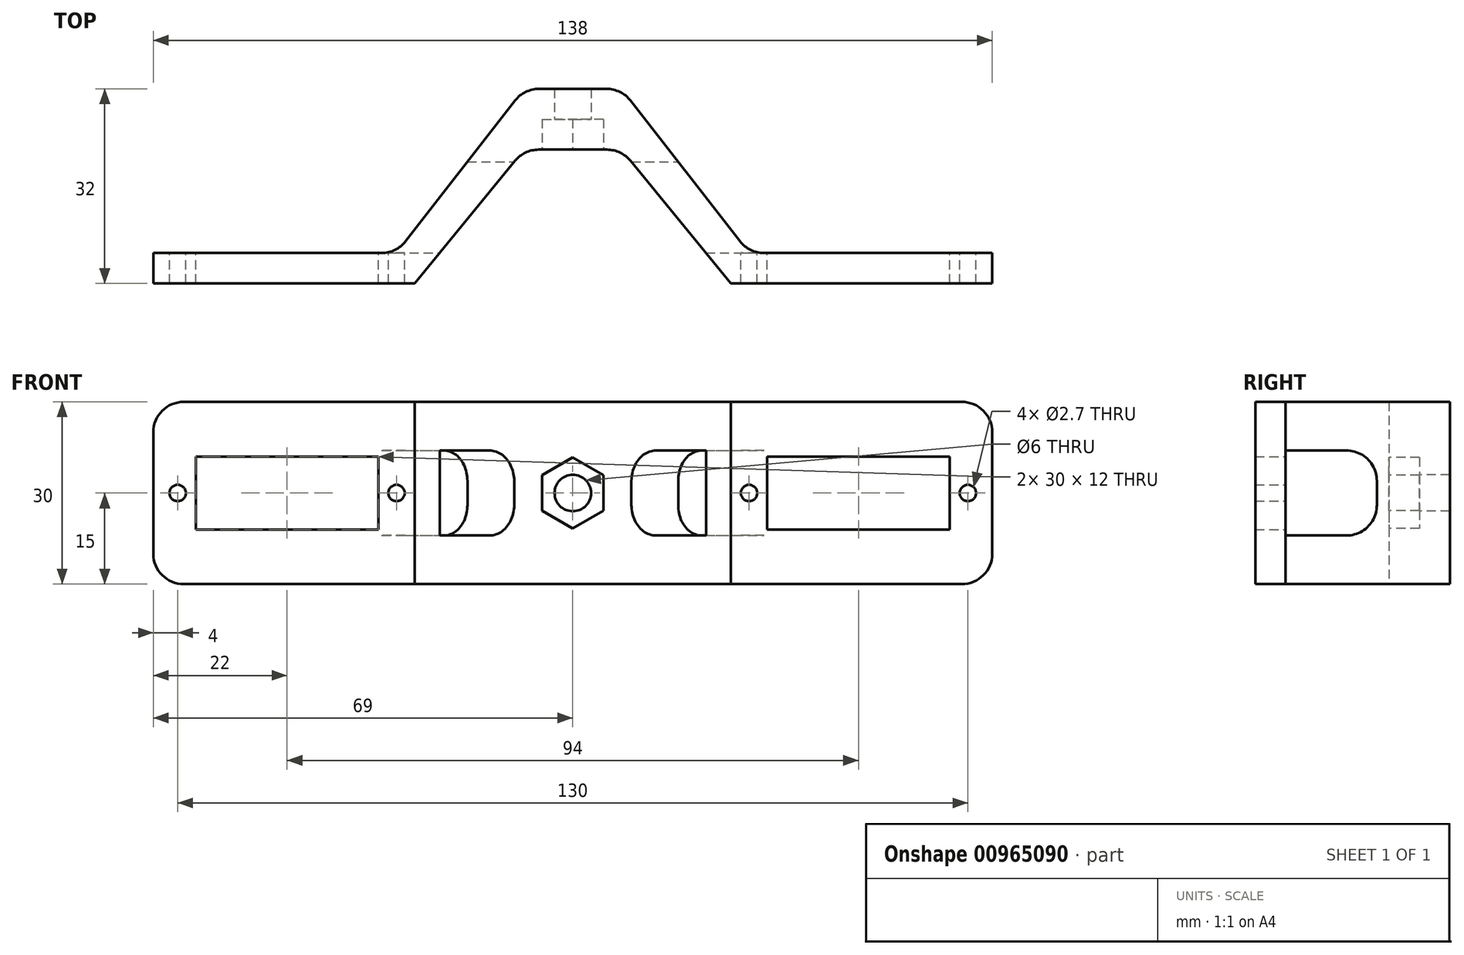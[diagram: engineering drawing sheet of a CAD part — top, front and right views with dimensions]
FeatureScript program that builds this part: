
annotation { "Feature Type Name" : "Feature", "Feature Type Description" : "" }
export const myFeature = defineFeature(function(context is Context, id is Id, definition is map)
    precondition{}
    {
        {
            var Q0;
            Q0=qCreatedBy(makeId("Top.planeOp"),FACE);
            var sketch = newSketch(context, id + "F0", { "sketchPlane" : qUnion([Q0])});
            skLineSegment(sketch, "E0", {"start": v(8, 32) * mm, "end": v(-8, 32) * mm});
            skLineSegment(sketch, "E1", {"start": v(-8, 32) * mm, "end": v(-29, 5) * mm});
            skLineSegment(sketch, "E2", {"start": v(-29, 5) * mm, "end": v(-69, 5) * mm});
            skLineSegment(sketch, "E3", {"start": v(-69, 5) * mm, "end": v(-69, 0) * mm});
            skLineSegment(sketch, "E4", {"start": v(69, 0) * mm, "end": v(69, 5) * mm});
            skLineSegment(sketch, "E5", {"start": v(69, 5) * mm, "end": v(29, 5) * mm});
            skLineSegment(sketch, "E6", {"start": v(29, 5) * mm, "end": v(8, 32) * mm});
            skLineSegment(sketch, "E7", {"start": v(-69, 0) * mm, "end": v(-26, 0) * mm});
            skLineSegment(sketch, "E8", {"start": v(-26, 0) * mm, "end": v(-8, 22) * mm});
            skLineSegment(sketch, "E9", {"start": v(-8, 22) * mm, "end": v(8, 22) * mm});
            skLineSegment(sketch, "E10", {"start": v(8, 22) * mm, "end": v(26, 0) * mm});
            skLineSegment(sketch, "E11", {"start": v(26, 0) * mm, "end": v(69, 0) * mm});
            skSolve(sketch);
        }
        {
            var Q0;
            Q0=makeQuery(id+"F0.imprint","IMPRINT",FACE,{"disambiguationData":[TD([[makeQuery(id+"F0.imprint","IMPRINT",EDGE,{"derivedFrom":sQuery(id+"F0.wireOp",EDGE,"E0")}),1.0]])]});
            extrude(context, id + "F1", {"entities" : qUnion([Q0]), "flatOperationType" : FlatOperationType.REMOVE, "depth" : 30 * mm, "offsetDistance" : 25 * mm, "domain" : OperationDomain.MODEL});
        }
        {
            var Q0;
            Q0=makeQuery(id+"F1.opExtrude","SWEPT_FACE",FACE,{"disambiguationData":[OSD([sQuery(id+"F0.wireOp",EDGE,"E5")])]});
            var sketch = newSketch(context, id + "F2", { "sketchPlane" : qUnion([Q0])});
            skLineSegment(sketch, "E12.bottom", {"start": v(62, 9) * mm, "end": v(32, 9) * mm});
            skLineSegment(sketch, "E12.top", {"start": v(62, 21) * mm, "end": v(32, 21) * mm});
            skLineSegment(sketch, "E12.left", {"start": v(62, 9) * mm, "end": v(62, 21) * mm});
            skLineSegment(sketch, "E12.right", {"start": v(32, 9) * mm, "end": v(32, 21) * mm});
            skLineSegment(sketch, "E13.bottom", {"start": v(-32, 9) * mm, "end": v(-62, 9) * mm});
            skLineSegment(sketch, "E13.top", {"start": v(-32, 21) * mm, "end": v(-62, 21) * mm});
            skLineSegment(sketch, "E13.left", {"start": v(-32, 9) * mm, "end": v(-32, 21) * mm});
            skLineSegment(sketch, "E13.right", {"start": v(-62, 9) * mm, "end": v(-62, 21) * mm});
            skCircle(sketch, "E14", {"center": v(65, 15) * mm, "radius": 1.35 * mm});
            skCircle(sketch, "E15", {"center": v(29, 15) * mm, "radius": 1.35 * mm});
            skCircle(sketch, "E16", {"center": v(-65, 15) * mm, "radius": 1.35 * mm});
            skCircle(sketch, "E17", {"center": v(-29, 15) * mm, "radius": 1.35 * mm});
            skSolve(sketch);
        }
        {
            var Q0;
            Q0=makeQuery(id+"F1.opExtrude","SWEPT_FACE",FACE,{"disambiguationData":[OSD([sQuery(id+"F0.wireOp",EDGE,"E9")])]});
            var sketch = newSketch(context, id + "F3", { "sketchPlane" : qUnion([Q0])});
            skCircle(sketch, "E18", {"center": v(0, 15) * mm, "radius": 3 * mm});
            skCircle(sketch, "E19.cCircle", {"center": v(0, 15) * mm, "radius": 5.05 * mm, "construction": true});
            skLineSegment(sketch, "E19.0", {"start": v(5.05, 12.08) * mm, "end": v(0, 9.17) * mm});
            skLineSegment(sketch, "E19.1", {"start": v(0, 9.17) * mm, "end": v(-5.05, 12.08) * mm});
            skLineSegment(sketch, "E19.2", {"start": v(-5.05, 12.08) * mm, "end": v(-5.05, 17.92) * mm});
            skLineSegment(sketch, "E19.3", {"start": v(-5.05, 17.92) * mm, "end": v(0, 20.83) * mm});
            skLineSegment(sketch, "E19.4", {"start": v(0, 20.83) * mm, "end": v(5.05, 17.92) * mm});
            skLineSegment(sketch, "E19.5", {"start": v(5.05, 17.92) * mm, "end": v(5.05, 12.08) * mm});
            skPoint(sketch, "E19.0.midPoint", {"position": v(2.53, 10.63) * mm});
            skSolve(sketch);
        }
        {
            var Q0;
            Q0=makeQuery(id+"F3.imprint","IMPRINT",FACE,{"disambiguationData":[TD([[makeQuery(id+"F3.imprint","IMPRINT",EDGE,{"derivedFrom":sQuery(id+"F3.wireOp",EDGE,"E18")}),1.0]])]});
            extrude(context, id + "F4", {"entities" : qUnion([Q0]), "operationType" : NewBodyOperationType.REMOVE, "oppositeDirection" : true, "depth" : 25 * mm, "offsetDistance" : 25 * mm});
        }
        {
            var Q0;
            Q0=makeQuery(id+"F3.imprint","IMPRINT",FACE,{"disambiguationData":[TD([[makeQuery(id+"F3.imprint","IMPRINT",EDGE,{"derivedFrom":sQuery(id+"F3.wireOp",EDGE,"E18")}),-1.0]])]});
            var Q1;
            {var subQ0=sQuery(id+"F3.wireOp",EDGE,"BezBhqOi-Dq81-y19x-YtIC-0gsC98FfVjEG");var subQ1=sQuery(id+"F3.wireOp",EDGE,"ncgn8NgD-MM0d-W8xm-oQu1-WhMMswXOpPgE.bottom");var subQ2=makeQuery(id+"F3.imprint","INTERSECT",VERTEX,{"derivedFrom":[subQ1,subQ0]});Q1=makeQuery(id+"F3.imprint","IMPRINT",FACE,{"disambiguationData":[TD([[makeQuery(id+"F3.imprint","IMPRINT",EDGE,{"disambiguationData":[TD([[subQ2,-1.0]])],"derivedFrom":subQ1}),1.0]])]});}
            var Q2;
            {var subQ0=sQuery(id+"F3.wireOp",EDGE,"6shvffcE-fs8c-bkRR-tV69-GbnKZBFpZLUS");var subQ1=sQuery(id+"F3.wireOp",EDGE,"ncgn8NgD-MM0d-W8xm-oQu1-WhMMswXOpPgE.top");var subQ2=makeQuery(id+"F3.imprint","INTERSECT",VERTEX,{"derivedFrom":[subQ1,subQ0]});Q2=makeQuery(id+"F3.imprint","IMPRINT",FACE,{"disambiguationData":[TD([[makeQuery(id+"F3.imprint","IMPRINT",EDGE,{"disambiguationData":[TD([[subQ2,-1.0]])],"derivedFrom":subQ1}),-1.0]])]});}
            extrude(context, id + "F5", {"entities" : qUnion([Q0, Q1, Q2]), "operationType" : NewBodyOperationType.REMOVE, "oppositeDirection" : true, "depth" : 5 * mm, "offsetDistance" : 25 * mm});
        }
        {
            var Q0;
            Q0=makeQuery(id+"F1.opExtrude","SWEPT_FACE",FACE,{"disambiguationData":[OSD([sQuery(id+"F0.wireOp",EDGE,"E4")])]});
            var sketch = newSketch(context, id + "F6", { "sketchPlane" : qUnion([Q0])});
            skLineSegment(sketch, "E20.bottom", {"start": v(5, 22) * mm, "end": v(20, 22) * mm});
            skLineSegment(sketch, "E20.top", {"start": v(5, 8) * mm, "end": v(20, 8) * mm});
            skLineSegment(sketch, "E20.left", {"start": v(5, 22) * mm, "end": v(5, 8) * mm});
            skLineSegment(sketch, "E20.right", {"start": v(20, 22) * mm, "end": v(20, 8) * mm});
            skSolve(sketch);
        }
        {
            var Q0;
            Q0=makeQuery(id+"F6.imprint","IMPRINT",FACE,{"disambiguationData":[TD([[makeQuery(id+"F6.imprint","IMPRINT",EDGE,{"derivedFrom":sQuery(id+"F6.wireOp",EDGE,"E20.bottom")}),-1.0]])]});
            extrude(context, id + "F7", {"entities" : qUnion([Q0]), "operationType" : NewBodyOperationType.REMOVE, "oppositeDirection" : true, "depth" : 160 * mm, "offsetDistance" : 25 * mm});
        }
        {
            var Q0;
            Q0=makeQuery(id+"F1.opExtrude","SWEPT_EDGE",EDGE,{"disambiguationData":[OSD([sQuery(id+"F0.wireOp",EDGE,"E0"),sQuery(id+"F0.wireOp",EDGE,"E1")])]});
            var Q1;
            Q1=makeQuery(id+"F1.opExtrude","SWEPT_EDGE",EDGE,{"disambiguationData":[OSD([sQuery(id+"F0.wireOp",EDGE,"E0"),sQuery(id+"F0.wireOp",EDGE,"E6")])]});
            var Q2;
            Q2=makeQuery(id+"F1.opExtrude","SWEPT_EDGE",EDGE,{"disambiguationData":[OSD([sQuery(id+"F0.wireOp",EDGE,"E8"),sQuery(id+"F0.wireOp",EDGE,"E9")])]});
            var Q3;
            Q3=makeQuery(id+"F1.opExtrude","SWEPT_EDGE",EDGE,{"disambiguationData":[OSD([sQuery(id+"F0.wireOp",EDGE,"E9"),sQuery(id+"F0.wireOp",EDGE,"E10")])]});
            var Q4;
            {var subQ1=sQuery(id+"F0.wireOp",EDGE,"E6");var subQ2=makeQuery(id+"F1.opExtrude","SWEPT_FACE",FACE,{"disambiguationData":[OSD([subQ1])]});var subQ3=sQuery(id+"F0.wireOp",EDGE,"E5");var subQ4=makeQuery(id+"F1.opExtrude","SWEPT_FACE",FACE,{"disambiguationData":[OSD([subQ3])]});Q4=makeQuery(id+"F9.boolean.opBoolean","SPLIT",EDGE,{"disambiguationData":[topologyDisambiguationEdgeConnected([subQ4,subQ2]),TD([makeQuery(id+"F1.opExtrude","CAP_FACE",FACE,{"disambiguationData":[OSD([sQuery(id+"F0.wireOp",EDGE,"E0"),sQuery(id+"F0.wireOp",EDGE,"E1"),sQuery(id+"F0.wireOp",EDGE,"E2"),sQuery(id+"F0.wireOp",EDGE,"E3"),sQuery(id+"F0.wireOp",EDGE,"E4"),subQ3,subQ1,sQuery(id+"F0.wireOp",EDGE,"E7"),sQuery(id+"F0.wireOp",EDGE,"E8"),sQuery(id+"F0.wireOp",EDGE,"E9"),sQuery(id+"F0.wireOp",EDGE,"E10"),sQuery(id+"F0.wireOp",EDGE,"E11")])],"isStart":false})])],"derivedFrom":makeQuery(id+"F1.opExtrude","SWEPT_EDGE",EDGE,{"disambiguationData":[OSD([subQ3,subQ1])]})});}
            var Q5;
            {var subQ1=sQuery(id+"F0.wireOp",EDGE,"E6");var subQ2=makeQuery(id+"F1.opExtrude","SWEPT_FACE",FACE,{"disambiguationData":[OSD([subQ1])]});var subQ3=sQuery(id+"F0.wireOp",EDGE,"E5");var subQ4=makeQuery(id+"F1.opExtrude","SWEPT_FACE",FACE,{"disambiguationData":[OSD([subQ3])]});Q5=makeQuery(id+"F9.boolean.opBoolean","SPLIT",EDGE,{"disambiguationData":[topologyDisambiguationEdgeConnected([subQ4,subQ2]),TD([makeQuery(id+"F1.opExtrude","CAP_FACE",FACE,{"disambiguationData":[OSD([sQuery(id+"F0.wireOp",EDGE,"E0"),sQuery(id+"F0.wireOp",EDGE,"E1"),sQuery(id+"F0.wireOp",EDGE,"E2"),sQuery(id+"F0.wireOp",EDGE,"E3"),sQuery(id+"F0.wireOp",EDGE,"E4"),subQ3,subQ1,sQuery(id+"F0.wireOp",EDGE,"E7"),sQuery(id+"F0.wireOp",EDGE,"E8"),sQuery(id+"F0.wireOp",EDGE,"E9"),sQuery(id+"F0.wireOp",EDGE,"E10"),sQuery(id+"F0.wireOp",EDGE,"E11")])],"isStart":true})])],"derivedFrom":makeQuery(id+"F1.opExtrude","SWEPT_EDGE",EDGE,{"disambiguationData":[OSD([subQ3,subQ1])]})});}
            var Q6;
            {var subQ0=sQuery(id+"F6.wireOp",EDGE,"E20.top");var subQ1=sQuery(id+"F6.wireOp",EDGE,"E20.right");Q6=makeQuery(id+"F7.boolean.opBoolean","COPY",EDGE,{"disambiguationData":[TD([makeQuery(id+"F1.opExtrude","SWEPT_FACE",FACE,{"disambiguationData":[OSD([sQuery(id+"F0.wireOp",EDGE,"E6")])]})])],"derivedFrom":makeQuery(id+"F7.opExtrude","SWEPT_EDGE",EDGE,{"disambiguationData":[OSD([subQ0,subQ1])]})});}
            var Q7;
            {var subQ0=sQuery(id+"F6.wireOp",EDGE,"E20.bottom");var subQ1=sQuery(id+"F6.wireOp",EDGE,"E20.right");Q7=makeQuery(id+"F7.boolean.opBoolean","COPY",EDGE,{"disambiguationData":[TD([makeQuery(id+"F1.opExtrude","SWEPT_FACE",FACE,{"disambiguationData":[OSD([sQuery(id+"F0.wireOp",EDGE,"E6")])]})])],"derivedFrom":makeQuery(id+"F7.opExtrude","SWEPT_EDGE",EDGE,{"disambiguationData":[OSD([subQ0,subQ1])]})});}
            var Q8;
            {var subQ0=sQuery(id+"F6.wireOp",EDGE,"E20.top");var subQ1=sQuery(id+"F6.wireOp",EDGE,"E20.right");Q8=makeQuery(id+"F7.boolean.opBoolean","COPY",EDGE,{"disambiguationData":[TD([makeQuery(id+"F1.opExtrude","SWEPT_FACE",FACE,{"disambiguationData":[OSD([sQuery(id+"F0.wireOp",EDGE,"E1")])]})])],"derivedFrom":makeQuery(id+"F7.opExtrude","SWEPT_EDGE",EDGE,{"disambiguationData":[OSD([subQ0,subQ1])]})});}
            var Q9;
            {var subQ0=sQuery(id+"F6.wireOp",EDGE,"E20.bottom");var subQ1=sQuery(id+"F6.wireOp",EDGE,"E20.right");Q9=makeQuery(id+"F7.boolean.opBoolean","COPY",EDGE,{"disambiguationData":[TD([makeQuery(id+"F1.opExtrude","SWEPT_FACE",FACE,{"disambiguationData":[OSD([sQuery(id+"F0.wireOp",EDGE,"E1")])]})])],"derivedFrom":makeQuery(id+"F7.opExtrude","SWEPT_EDGE",EDGE,{"disambiguationData":[OSD([subQ0,subQ1])]})});}
            var Q10;
            {var subQ0=sQuery(id+"F0.wireOp",EDGE,"E2");var subQ1=makeQuery(id+"F1.opExtrude","SWEPT_FACE",FACE,{"disambiguationData":[OSD([subQ0])]});var subQ3=sQuery(id+"F0.wireOp",EDGE,"E1");var subQ4=makeQuery(id+"F1.opExtrude","SWEPT_FACE",FACE,{"disambiguationData":[OSD([subQ3])]});Q10=makeQuery(id+"F9.boolean.opBoolean","SPLIT",EDGE,{"disambiguationData":[topologyDisambiguationEdgeConnected([subQ4,subQ1]),TD([makeQuery(id+"F1.opExtrude","CAP_FACE",FACE,{"disambiguationData":[OSD([sQuery(id+"F0.wireOp",EDGE,"E0"),subQ3,subQ0,sQuery(id+"F0.wireOp",EDGE,"E3"),sQuery(id+"F0.wireOp",EDGE,"E4"),sQuery(id+"F0.wireOp",EDGE,"E5"),sQuery(id+"F0.wireOp",EDGE,"E6"),sQuery(id+"F0.wireOp",EDGE,"E7"),sQuery(id+"F0.wireOp",EDGE,"E8"),sQuery(id+"F0.wireOp",EDGE,"E9"),sQuery(id+"F0.wireOp",EDGE,"E10"),sQuery(id+"F0.wireOp",EDGE,"E11")])],"isStart":true})])],"derivedFrom":makeQuery(id+"F1.opExtrude","SWEPT_EDGE",EDGE,{"disambiguationData":[OSD([subQ3,subQ0])]})});}
            var Q11;
            {var subQ0=sQuery(id+"F0.wireOp",EDGE,"E2");var subQ1=makeQuery(id+"F1.opExtrude","SWEPT_FACE",FACE,{"disambiguationData":[OSD([subQ0])]});var subQ3=sQuery(id+"F0.wireOp",EDGE,"E1");var subQ4=makeQuery(id+"F1.opExtrude","SWEPT_FACE",FACE,{"disambiguationData":[OSD([subQ3])]});Q11=makeQuery(id+"F9.boolean.opBoolean","SPLIT",EDGE,{"disambiguationData":[topologyDisambiguationEdgeConnected([subQ4,subQ1]),TD([makeQuery(id+"F1.opExtrude","CAP_FACE",FACE,{"disambiguationData":[OSD([sQuery(id+"F0.wireOp",EDGE,"E0"),subQ3,subQ0,sQuery(id+"F0.wireOp",EDGE,"E3"),sQuery(id+"F0.wireOp",EDGE,"E4"),sQuery(id+"F0.wireOp",EDGE,"E5"),sQuery(id+"F0.wireOp",EDGE,"E6"),sQuery(id+"F0.wireOp",EDGE,"E7"),sQuery(id+"F0.wireOp",EDGE,"E8"),sQuery(id+"F0.wireOp",EDGE,"E9"),sQuery(id+"F0.wireOp",EDGE,"E10"),sQuery(id+"F0.wireOp",EDGE,"E11")])],"isStart":false})])],"derivedFrom":makeQuery(id+"F1.opExtrude","SWEPT_EDGE",EDGE,{"disambiguationData":[OSD([subQ3,subQ0])]})});}
            var Q12;
            Q12=makeQuery(id+"F1.opExtrude","CAP_EDGE",EDGE,{"disambiguationData":[OSD([sQuery(id+"F0.wireOp",EDGE,"E3")])],"isStart":false});
            var Q13;
            Q13=makeQuery(id+"F1.opExtrude","CAP_EDGE",EDGE,{"disambiguationData":[OSD([sQuery(id+"F0.wireOp",EDGE,"E3")])],"isStart":true});
            var Q14;
            Q14=makeQuery(id+"F1.opExtrude","CAP_EDGE",EDGE,{"disambiguationData":[OSD([sQuery(id+"F0.wireOp",EDGE,"E4")])],"isStart":false});
            var Q15;
            Q15=makeQuery(id+"F1.opExtrude","CAP_EDGE",EDGE,{"disambiguationData":[OSD([sQuery(id+"F0.wireOp",EDGE,"E4")])],"isStart":true});
            fillet(context, id + "F8", {"entities" : qUnion([Q0, Q1, Q2, Q3, Q4, Q5, Q6, Q7, Q8, Q9, Q10, Q11, Q12, Q13, Q14, Q15]), "radius" : 5 * mm, "tangentPropagation" : true, "defaultsChanged" : true, "vertexSettings" : [], "allowEdgeOverflow" : false});
        }
        {
            var Q0;
            Q0=makeQuery(id+"F2.imprint","IMPRINT",FACE,{"disambiguationData":[TD([[makeQuery(id+"F2.imprint","IMPRINT",EDGE,{"derivedFrom":sQuery(id+"F2.wireOp",EDGE,"E12.bottom")}),-1.0]])]});
            var Q1;
            Q1=makeQuery(id+"F2.imprint","IMPRINT",FACE,{"disambiguationData":[TD([[makeQuery(id+"F2.imprint","IMPRINT",EDGE,{"derivedFrom":sQuery(id+"F2.wireOp",EDGE,"E13.bottom")}),-1.0]])]});
            var Q2;
            Q2=makeQuery(id+"F2.imprint","IMPRINT",FACE,{"disambiguationData":[TD([[makeQuery(id+"F2.imprint","IMPRINT",EDGE,{"derivedFrom":sQuery(id+"F2.wireOp",EDGE,"E17")}),1.0]])]});
            var Q3;
            Q3=makeQuery(id+"F2.imprint","IMPRINT",FACE,{"disambiguationData":[TD([[makeQuery(id+"F2.imprint","IMPRINT",EDGE,{"derivedFrom":sQuery(id+"F2.wireOp",EDGE,"E16")}),1.0]])]});
            var Q4;
            Q4=makeQuery(id+"F2.imprint","IMPRINT",FACE,{"disambiguationData":[TD([[makeQuery(id+"F2.imprint","IMPRINT",EDGE,{"derivedFrom":sQuery(id+"F2.wireOp",EDGE,"E15")}),1.0]])]});
            var Q5;
            Q5=makeQuery(id+"F2.imprint","IMPRINT",FACE,{"disambiguationData":[TD([[makeQuery(id+"F2.imprint","IMPRINT",EDGE,{"derivedFrom":sQuery(id+"F2.wireOp",EDGE,"E14")}),1.0]])]});
            extrude(context, id + "F9", {"entities" : qUnion([Q0, Q1, Q2, Q3, Q4, Q5]), "operationType" : NewBodyOperationType.REMOVE, "oppositeDirection" : true, "depth" : 25 * mm, "offsetDistance" : 25 * mm});
        }
    });
